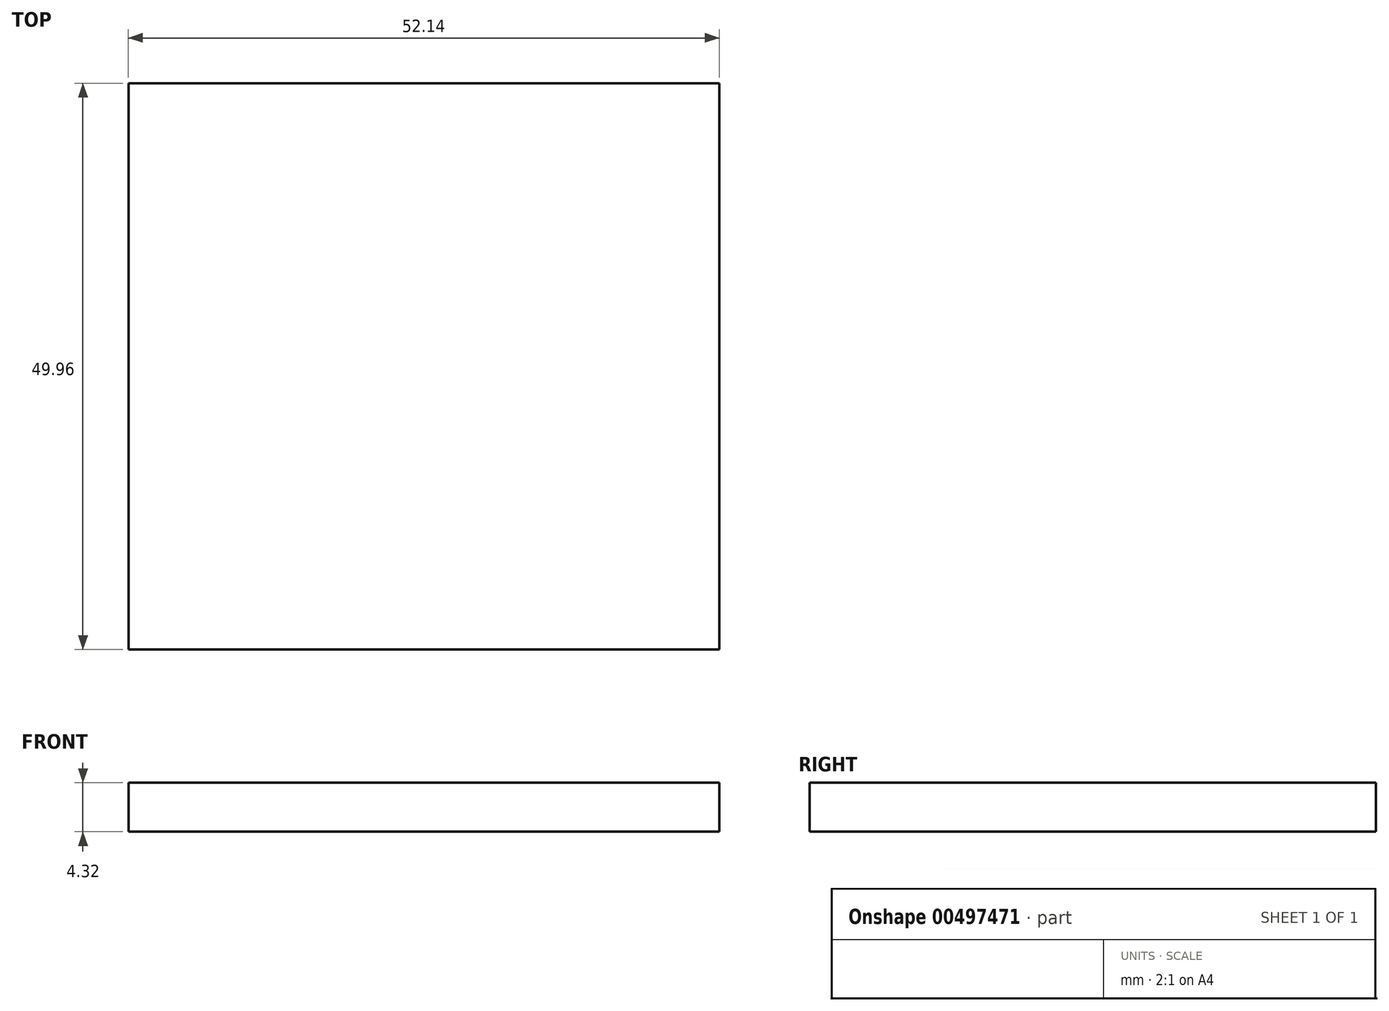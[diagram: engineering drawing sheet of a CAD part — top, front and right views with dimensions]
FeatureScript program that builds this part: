
annotation { "Feature Type Name" : "Feature", "Feature Type Description" : "" }
export const myFeature = defineFeature(function(context is Context, id is Id, definition is map)
    precondition{}
    {
        {
            var Q0;
            Q0=qCreatedBy(makeId("Top.planeOp"),FACE);
            var sketch = newSketch(context, id + "F0", { "sketchPlane" : qUnion([Q0])});
            skLineSegment(sketch, "E0", {"start": v(-120.4, -44.6) * mm, "end": v(-68.27, -44.6) * mm});
            skLineSegment(sketch, "E1", {"start": v(-68.27, -44.6) * mm, "end": v(-68.27, 5.36) * mm});
            skLineSegment(sketch, "E2", {"start": v(-68.27, 5.36) * mm, "end": v(-133.1, 5.36) * mm});
            skLineSegment(sketch, "E3", {"start": v(-133.1, 5.36) * mm, "end": v(-68.27, 5.36) * mm});
            skLineSegment(sketch, "E4", {"start": v(-68.27, -44.6) * mm, "end": v(-120.4, -44.6) * mm});
            skLineSegment(sketch, "E5", {"start": v(-120.4, -44.6) * mm, "end": v(-120.4, 5.36) * mm});
            skLineSegment(sketch, "E6", {"start": v(-120.4, 5.36) * mm, "end": v(-120.4, -44.6) * mm});
            skSolve(sketch);
        }
        {
            var Q0;
            Q0 = qSketchRegion(id + "F0", true);
            extrude(context, id + "F1", {"entities" : qUnion([Q0]), "depth" : 4.32 * mm});
        }
    });
